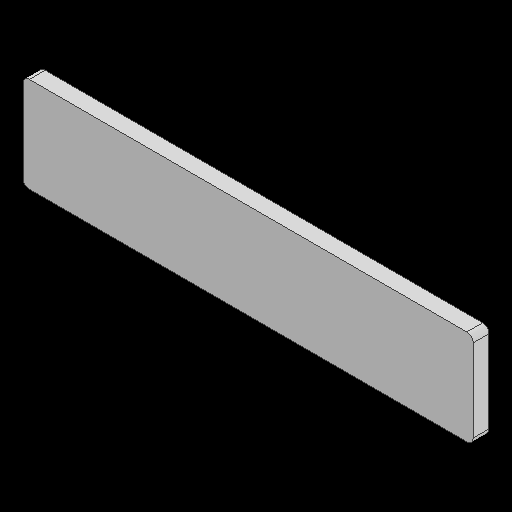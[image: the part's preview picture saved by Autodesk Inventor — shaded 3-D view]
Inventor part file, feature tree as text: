
AUTODESK INVENTOR PART (.ipt)
format: ipt  version: 2025.1 (Build 291241000, 241)  size: 142,336 bytes
history: native  units: in
note: dims shown in document units (in); Inventor stores cm internally (conversion verified against a paired STEP export)
features: other x2, extrude x2, sketch x2, fillet x1, projected_geometry x1
ambient origin geometry x8: Origin, YZ Plane, XZ Plane, XY Plane, X Axis, Y Axis, Z Axis, Center Point
bodies: Body1 (feature_tree)
feature tree (8):
  other  "솔리드1"
  extrude  "돌출1"  Depth=5.5906in
  extrude  "돌출2"  Depth=1.1811in
  fillet  "모깎기1"  Radius=0.0787in
  sketch  "스케치1"
  other  "스케치 - 직사각형 패턴1"
  sketch  "스케치2"
  projected_geometry  "투영된 루프1"
